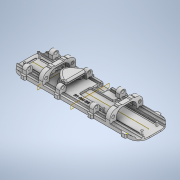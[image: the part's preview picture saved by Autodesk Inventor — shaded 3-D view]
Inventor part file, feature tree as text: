
AUTODESK INVENTOR PART (.ipt)
format: ipt  version: 2021 (Build 250183000, 183)  size: 3,272,704 bytes
history: native  units: in
note: dims shown in document units (in); Inventor stores cm internally (conversion verified against a paired STEP export)
features: fillet x17, extrude x16, sketch x16, mirror x10, plane x3, chamfer x1, revolve x1
ambient origin geometry x8: Origin, YZ Plane, XZ Plane, XY Plane, X Axis, Y Axis, Z Axis, Center Point
bodies: Solid1 (feature_tree)
feature tree (64):
  extrude  "Extrusion1"  Depth=4.9606in
  extrude  "Extrusion2"  TaperAngle=0.0deg  [1 undecoded]
  plane  "Work Plane1"
  plane  "Work Plane2"
  extrude  "Extrusion5"  Depth=0.2362in
  fillet  "Fillet2"  Radius=0.0787in
  mirror  "Mirror3"
  extrude  "Extrusion6"  TaperAngle=0.0deg  [1 undecoded]
  extrude  "Extrusion7"  Depth=0.2362in
  extrude  "Extrusion9"  [1 undecoded]
  extrude  "Extrusion10"  Depth=0.5354in
  fillet  "Fillet4"  Radius=0.9449in
  mirror  "Mirror4"
  mirror  "Mirror5"
  fillet  "Fillet5"  Radius=2.7559in
  fillet  "Fillet6"  Radius=0.4724in
  extrude  "Extrusion12"  Depth=0.0866in TaperAngle=0.0deg
  extrude  "Extrusion13"  Depth=0.0945in
  mirror  "Mirror8"
  mirror  "Mirror9"
  mirror  "Mirror10"
  fillet  "Fillet9"  Radius=0.0945in
  fillet  "Fillet12"  Radius=0.0945in
  extrude  "Extrusion17"  TaperAngle=0.0deg  [1 undecoded]
  fillet  "Fillet16"  [1 undecoded]
  mirror  "Mirror13"
  extrude  "Extrusion11"  Depth=0.7in
  plane  "Work Plane4"
  sketch  "Sketch52"  dims[d41=0.0in d42=0.0in d43=0.0in]
  extrude  "Extrusion24"  Depth=0.35in
  chamfer  "Chamfer7"  Distance=0.1575in
  extrude  "Extrusion25"  Depth=0.9449in
  extrude  "Extrusion26"  Depth=1.7087in
  fillet  "Fillet32"  Radius=0.0945in
  mirror  "Mirror19"
  mirror  "Mirror20"
  mirror  "Mirror21"
  extrude  "Extrusion28"  Depth=0.0945in
  extrude  "Extrusion29"  TaperAngle=0.0deg  [1 undecoded]
  revolve  "Revolution10"  [1 undecoded]
  fillet  "Fillet36"  [1 undecoded]
  fillet  "Fillet37"  [1 undecoded]
  fillet  "Fillet38"  Radius=0.9in
  fillet  "Fillet39"  Radius=0.7in
  fillet  "Fillet40"  Radius=0.35in
  fillet  "Fillet41"  Radius=0.1969in
  fillet  "Fillet42"  Radius=0.4094in
  fillet  "Fillet45"  [1 undecoded]
  fillet  "Fillet46"  [1 undecoded]
  sketch  "Sketch1"  dims[d0=0.1575in d1=0.0in d2=4.9606in]
  sketch  "Sketch2"  dims[d3=1.5512in d4=0.0in]
  sketch  "Sketch7"  dims[d5=0.0in d6=0.2362in d7=0.0787in d8=0.0in]
  sketch  "Sketch8"  dims[d15=-0.7756in d16=0.0in]
  sketch  "Sketch13"  dims[d17=0.0in d18=0.2362in]
  sketch  "Sketch14"  dims[d19=1.3386in d24=-2.4803in]
  sketch  "Sketch15"  dims[d28=0.5354in d29=0.0in d30=0.5354in d31=0.9449in d32=2.7559in d33=0.4724in]
  sketch  "Sketch25"  dims[d34=0.811in d35=0.0866in d36=0.0in]
  sketch  "Sketch39"  dims[d37=0.0945in d38=0.0945in d39=0.0945in d40=0.0945in]
  sketch  "Sketch53"  dims[d44=0.0in d45=0.7in]
  sketch  "Sketch54"  dims[d46=1.8in d47=0.35in d48=0.1575in d49=0.0in]
  sketch  "Sketch55"  dims[d60=1.9685in d61=0.9449in]
  sketch  "Sketch58"  dims[d62=0.4724in d63=1.7087in d64=0.0945in]
  sketch  "Sketch59"  dims[d65=0.0945in d66=0.0945in]
  sketch  "Sketch60"  dims[d67=0.0945in d68=0.0in d69=0.0in d70=0.0in d71=0.0in d72=0.9in d73=0.7in d74=0.35in d75=0.1969in d79=0.4094in d80=0.0in d81=0.0in d82=0.0in d83=0.0in d84=0.0in d85=0.0787in d86=0.0in d88=0.3543in d89=0.315in d92=0.0394in d93=0.0in d96=1.1024in d97=0.5512in d98=0.2756in d99=0.0787in d116=0.2362in d117=0.0in d118=0.0in d119=0.1181in d120=0.0394in d121=0.0in d126=0.1417in d127=1.5748in d128=0.0in d131=0.0394in d134=0.0in d138=0.5709in d148=0.0591in d171=0.0866in d172=0.0394in d173=0.0394in d174=0.0866in d175=0.2638in d176=0.0866in d177=0.0945in d178=0.0866in d179=0.0394in d180=0.0394in d181=0.0787in d182=0.0236in d183=0.0in d184=0.0433in d204=0.0945in d263=0.8661in d264=0.4331in d278=4.7244in d279=0.0in d285=0.0in d286=0.0in d288=-1.5748in d289=0.3937in d291=0.1969in d292=0.1181in d293=0.0in d298=0.0394in d299=0.2362in d300=45.0deg d301=0.4016in d302=0.0in d303=0.1969in d304=0.0197in d305=0.1417in d306=0.0in d307=0.0in d308=0.0886in d309=0.1441in d310=0.3937in d318=0.1516in d319=0.2883in d321=0.1417in d327=0.0in d328=0.0in d329=0.0in d330=0.126in d331=0.126in d332=0.315in d333=0.7087in d334=0.3543in d335=0.3937in d336=0.0in d337=0.1772in d338=0.1969in d339=0.0in d340=0.5906in d341=180.0deg d342=0.0in d343=0.0in d348=0.0787in d349=0.0787in d350=0.0787in d351=0.0551in d352=0.0551in d353=0.0551in d354=0.0551in d357=0.0551in d358=0.0472in d146=0.0197in d147=0.0344in d149=0.0344in d211=0.0197in d212=0.0344in d213=0.0197in d214=0.0344in d287=0.0197in]
note: 11 required parameter values undecoded (feature->parameter linkage not recoverable at this tier; creation-order binding heuristic only, values carry confidence <= 0.55)